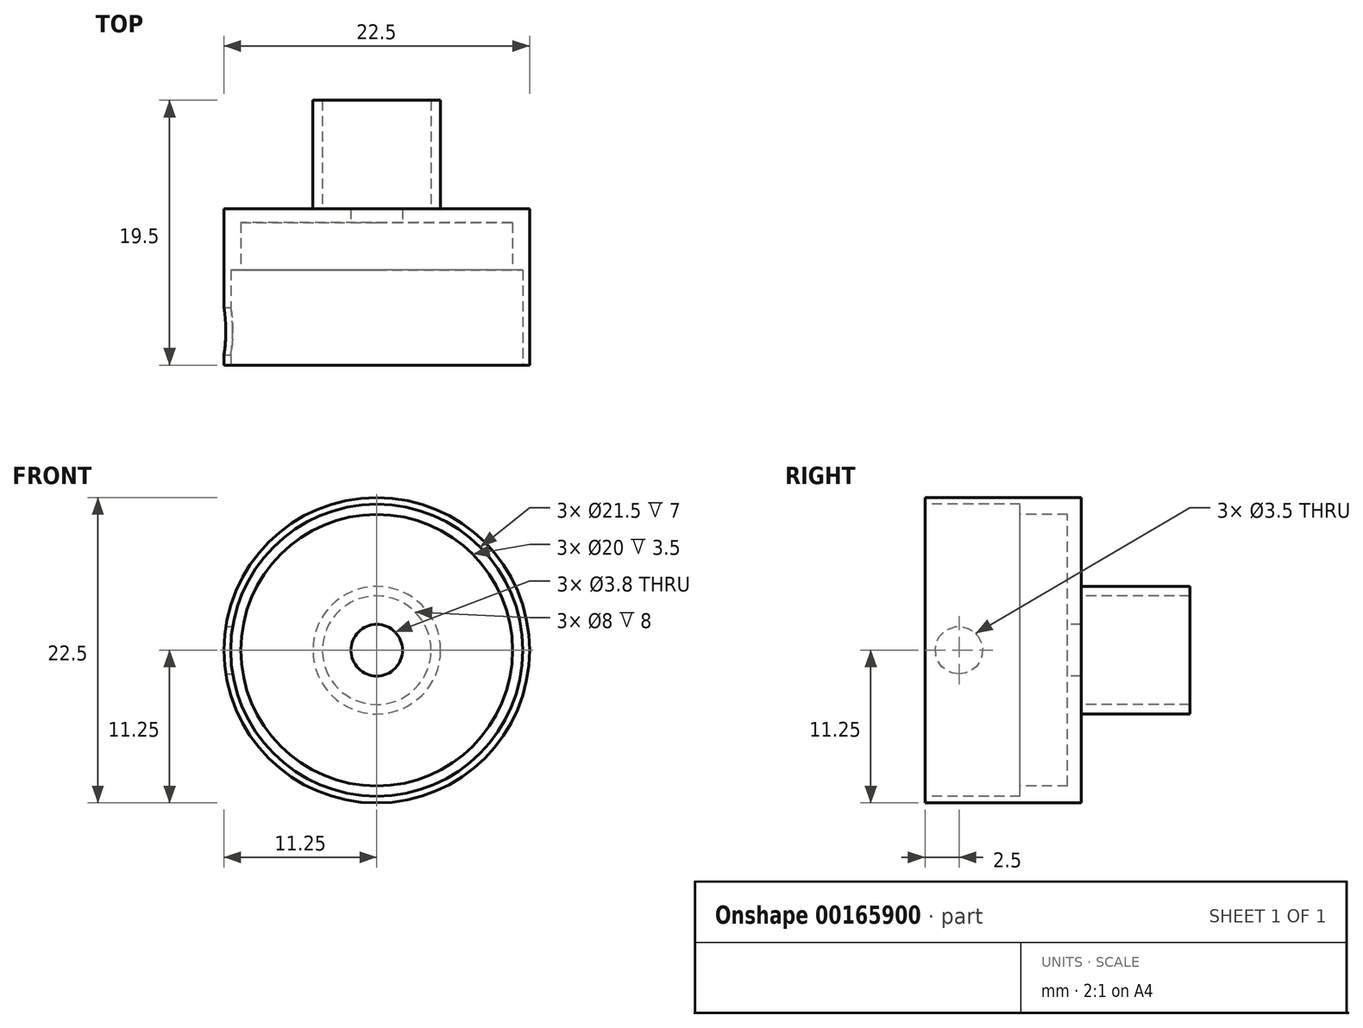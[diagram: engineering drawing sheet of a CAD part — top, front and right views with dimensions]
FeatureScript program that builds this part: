
annotation { "Feature Type Name" : "Feature", "Feature Type Description" : "" }
export const myFeature = defineFeature(function(context is Context, id is Id, definition is map)
    precondition{}
    {
        {
            var Q0;
            Q0=qCreatedBy(makeId("Right.planeOp"),FACE);
            var sketch = newSketch(context, id + "F0", { "sketchPlane" : qUnion([Q0])});
            skLineSegment(sketch, "E0", {"start": v(0, 0) * mm, "end": v(26.9, 0) * mm, "construction": true});
            skLineSegment(sketch, "E1", {"start": v(0, 11.25) * mm, "end": v(11.5, 11.25) * mm});
            skLineSegment(sketch, "E2", {"start": v(11.5, 11.25) * mm, "end": v(11.5, 4.7) * mm});
            skLineSegment(sketch, "E3", {"start": v(11.5, 4.7) * mm, "end": v(19.5, 4.7) * mm});
            skLineSegment(sketch, "E4", {"start": v(19.5, 4.7) * mm, "end": v(19.5, 4) * mm});
            skLineSegment(sketch, "E5", {"start": v(19.5, 4) * mm, "end": v(11.5, 4) * mm});
            skLineSegment(sketch, "E6", {"start": v(11.5, 4) * mm, "end": v(11.5, 1.9) * mm});
            skLineSegment(sketch, "E7", {"start": v(11.5, 1.9) * mm, "end": v(10.5, 1.9) * mm});
            skLineSegment(sketch, "E8", {"start": v(10.5, 1.9) * mm, "end": v(10.5, 10) * mm});
            skLineSegment(sketch, "E9", {"start": v(10.5, 10) * mm, "end": v(7, 10) * mm});
            skLineSegment(sketch, "E10", {"start": v(7, 10) * mm, "end": v(7, 10.75) * mm});
            skLineSegment(sketch, "E11", {"start": v(7, 10.75) * mm, "end": v(0, 10.75) * mm});
            skLineSegment(sketch, "E12", {"start": v(0, 10.75) * mm, "end": v(0, 11.25) * mm});
            skSolve(sketch);
        }
        {
            var Q0;
            Q0=makeQuery(id+"F0.imprint","IMPRINT",FACE,{"disambiguationData":[TD([[makeQuery(id+"F0.imprint","IMPRINT",EDGE,{"derivedFrom":sQuery(id+"F0.wireOp",EDGE,"E1")}),-1.0]])]});
            var Q1;
            Q1=sQuery(id+"F0.wireOp",EDGE,"E0");
            revolve(context, id + "F1", {"entities" : qUnion([Q0]), "axis" : qUnion([Q1]), "revolveType" : RevolveType.FULL});
        }
        {
            var Q0;
            Q0=qCreatedBy(makeId("Right.planeOp"),FACE);
            var sketch = newSketch(context, id + "F2", { "sketchPlane" : qUnion([Q0])});
            skCircle(sketch, "E13", {"center": v(2.5, 0) * mm, "radius": 1.75 * mm});
            skSolve(sketch);
        }
        {
            var Q0;
            Q0=makeQuery(id+"F2.imprint","IMPRINT",FACE,{"disambiguationData":[TD([[makeQuery(id+"F2.imprint","IMPRINT",EDGE,{"derivedFrom":sQuery(id+"F2.wireOp",EDGE,"E13")}),1.0]])]});
            extrude(context, id + "F3", {"entities" : qUnion([Q0]), "operationType" : NewBodyOperationType.REMOVE, "endBound" : BoundingType.THROUGH_ALL, "oppositeDirection" : true, "depth" : 25 * mm});
        }
    });
